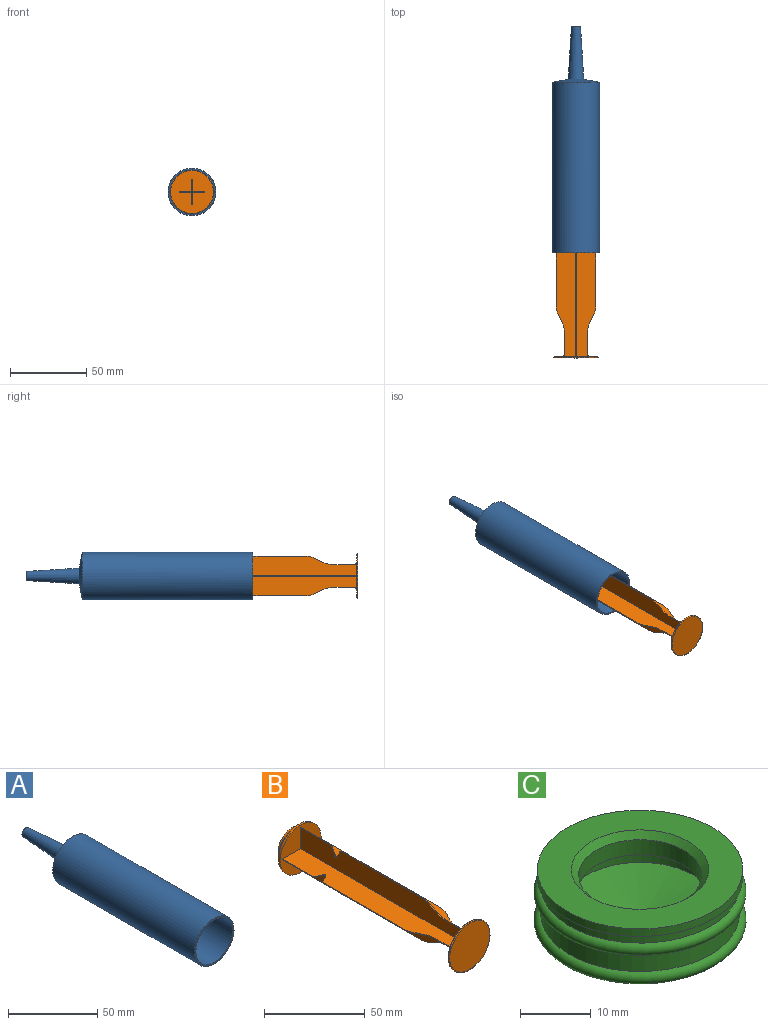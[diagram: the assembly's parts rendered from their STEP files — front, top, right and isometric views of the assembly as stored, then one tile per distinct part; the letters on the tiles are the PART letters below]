
ASSEMBLY  parts=3 mates=2
PART A: 8 faces, bbox 31.2x149x31.2 mm
  f0: cylinder r=14.5mm len=111mm, axis (0,-1,0), area 10112.8mm2, adj f1,f3
  f1: plane 31.2x31.2mm, normal (0,-1,0), area 104mm2, adj f0,f2
  f2: cylinder r=15.6mm len=112.04mm, axis (0,-1,0), area 10981.6mm2, adj f1,f5
  f3: plane 29x29mm, normal (0,-1,0), area 588.1mm2, adj f0,f7
  f4: plane 6x6mm, normal (0,1,0), area 12mm2, adj f6,f7
  f5: cone r=5.5mm half-angle=79deg, axis (0,-1,0), area 694.4mm2, adj f2,f6
  f6: cone r=3mm half-angle=3.5deg, axis (0,-1,0), area 894.5mm2, adj f4,f5
  f7: cone r=4.8mm half-angle=3.8deg, axis (0,-1,0), area 846.6mm2, adj f3,f4
PART B: 103 faces, bbox 31.4x126.4x31.4 mm
  f0: plane 28.8x28.8mm, normal (0,-1,0), area 630.8mm2, adj f4,f5,f17,f23,f61,f62,f63,f64
  f1: plane 20x20mm, normal (0,1,0), area 299.9mm2, adj f2,f3,f28,f30,f35,f36,f37,f38
  f2: plane 8.8x1.47mm, normal (0,0,1), area 6.5mm2, adj f1,f3,f42
  f3: plane 8.8x1.47mm, normal (0.16,0.99,0), area 3.6mm2, adj f1,f2,f30,f48
  f4: plane 118.15x12.8mm, normal (0,0,1), area 1355.9mm2, adj f0,f7,f11,f12,f13,f14,f15,f16
  f5: plane 118.15x12.8mm, normal (0,0,-1), area 1355.9mm2, adj f0,f7,f11,f12,f13,f14,f15,f16
  f6: cylinder r=14.5mm len=29mm, axis (0,-1,0), area 4.6mm2, adj f9,f10
  f7: plane 28.2x28.2mm, normal (0,1,0), area 611.1mm2, adj f4,f5,f10,f11,f61,f62,f63,f64
  f8: plane 28.2x28.2mm, normal (0,-1,0), area 624.6mm2, adj f9
  f9: torus R=14.1mm, axis (0,1,0), area 56.7mm2, adj f6,f8
  f10: torus R=14.1mm, axis (0,1,0), area 56.7mm2, adj f6,f7
  f11: cylinder r=2.28mm len=1.54mm, axis (0,0,-1), area 0.8mm2, adj f4,f5,f7,f12
  f12: plane 14.07x0.4mm, normal (1,0,0), area 5.6mm2, adj f4,f5,f11,f18
  f13: plane 4.67x2.33mm, normal (0.89,-0.45,0), area 2.1mm2, adj f4,f5,f18,f19
  f14: plane 54.93x0.4mm, normal (1,0,0), area 22mm2, adj f4,f5,f19,f22
  f15: plane 4x2.03mm, normal (0.45,0.89,0), area 1.8mm2, adj f4,f5,f20,f22
  f16: plane 4x2.03mm, normal (0.45,-0.89,0), area 1.8mm2, adj f4,f5,f20,f21
  f17: plane 20.47x0.4mm, normal (1,0,0), area 8.2mm2, adj f0,f4,f5,f21
  f18: cylinder r=15mm len=6.71mm, axis (0,0,1), area 2.8mm2, adj f4,f5,f12,f13
  f19: cylinder r=15mm len=6.71mm, axis (0,0,-1), area 2.8mm2, adj f4,f5,f13,f14
  f20: cylinder r=0.8mm len=1.43mm, axis (0,0,-1), area 0.7mm2, adj f4,f5,f15,f16
  f21: cylinder r=2mm len=1.78mm, axis (0,0,-1), area 0.9mm2, adj f4,f5,f16,f17
  f22: cylinder r=2mm len=1.78mm, axis (0,0,1), area 0.9mm2, adj f4,f5,f14,f15
  f23: cylinder r=14.4mm len=28.8mm, axis (0,-1,0), area 108.6mm2, adj f0,f24
  f24: plane 28.8x28.8mm, normal (0,1,0), area 640.1mm2, adj f23,f25,f26,f27,f52,f53,f54,f55
  f25: plane 7x3.7mm, normal (0,0,-1), area 25.9mm2, adj f24,f27,f29,f52
  f26: plane 7x3.7mm, normal (0,0,1), area 25.9mm2, adj f24,f27,f29,f59
  f27: plane 3.7x0.4mm, normal (1,0,0), area 1.5mm2, adj f24,f25,f26,f29
  f28: cylinder r=10mm len=20mm, axis (0,1,0), area 62.8mm2, adj f1,f29
  f29: plane 20x20mm, normal (0,-1,0), area 302.8mm2, adj f25,f26,f27,f28,f52,f53,f54,f55
  f30: plane 8.8x1.47mm, normal (0,0,-1), area 6.5mm2, adj f1,f3,f35
  f31: plane 0.4x0.03mm, normal (-1,0,0), area 0mm2, adj f32,f33,f37
  f32: plane 0.2x0.2mm, normal (0,0.99,0.16), area 0mm2, adj f31,f33,f41
  f33: plane 0.2x0.2mm, normal (0,0.99,-0.16), area 0mm2, adj f31,f32,f34
  f34: plane 0.2x0.2mm, normal (-0.16,0.99,0), area 0mm2, adj f33,f45,f46
  f35: plane 8.8x1.47mm, normal (1,0,0), area 6.5mm2, adj f1,f30,f36
  f36: plane 8.8x1.47mm, normal (0,0.99,-0.16), area 3.6mm2, adj f1,f35,f44,f46
  f37: plane 8.8x1.47mm, normal (-0.16,0.99,0), area 3.6mm2, adj f1,f31,f38,f39
  f38: plane 8.8x1.47mm, normal (0,0,-1), area 6.5mm2, adj f1,f37,f44
  f39: plane 8.8x1.47mm, normal (0,0,1), area 6.5mm2, adj f1,f37,f43
  f40: plane 8.8x1.47mm, normal (0,0.99,0.16), area 3.6mm2, adj f1,f42,f43,f51
  f41: plane 0.2x0.2mm, normal (-0.16,0.99,0), area 0mm2, adj f32,f50,f51
  f42: plane 8.8x1.47mm, normal (1,0,0), area 6.5mm2, adj f1,f2,f40
  f43: plane 8.8x1.47mm, normal (-1,0,0), area 6.5mm2, adj f1,f39,f40
  f44: plane 8.8x1.47mm, normal (-1,0,0), area 6.5mm2, adj f1,f36,f38
  f45: plane 0.2x0.2mm, normal (0.16,0.99,0), area 0mm2, adj f34,f46,f49
  f46: plane 0.4x0.03mm, normal (0,0,-1), area 0mm2, adj f34,f36,f45
  f47: plane 0.2x0.2mm, normal (0,0.99,0.16), area 0mm2, adj f48,f49,f50
  f48: plane 0.4x0.03mm, normal (1,0,0), area 0mm2, adj f3,f47,f49
  f49: plane 0.2x0.2mm, normal (0,0.99,-0.16), area 0mm2, adj f45,f47,f48
  f50: plane 0.2x0.2mm, normal (0.16,0.99,0), area 0mm2, adj f41,f47,f51
  f51: plane 0.4x0.03mm, normal (0,0,1), area 0mm2, adj f40,f41,f50
  f52: plane 7x3.7mm, normal (1,0,0), area 25.9mm2, adj f24,f25,f29,f60
  f53: plane 3.7x0.4mm, normal (0,0,1), area 1.5mm2, adj f24,f29,f57,f59
  f54: plane 7x3.7mm, normal (0,0,-1), area 25.9mm2, adj f24,f29,f55,f58
  f55: plane 3.7x0.4mm, normal (-1,0,0), area 1.5mm2, adj f24,f29,f54,f56
  f56: plane 7x3.7mm, normal (0,0,1), area 25.9mm2, adj f24,f29,f55,f57
  f57: plane 7x3.7mm, normal (-1,0,0), area 25.9mm2, adj f24,f29,f53,f56
  f58: plane 7x3.7mm, normal (-1,0,0), area 25.9mm2, adj f24,f29,f54,f60
  f59: plane 7x3.7mm, normal (1,0,0), area 25.9mm2, adj f24,f26,f29,f53
  f60: plane 3.7x0.4mm, normal (0,0,-1), area 1.5mm2, adj f24,f29,f52,f58
  f61: plane 118.15x12.8mm, normal (-1,0,0), area 1355.9mm2, adj f0,f7,f64,f67,f68,f69,f70,f71
  f62: plane 118.15x12.8mm, normal (-1,0,0), area 1355.9mm2, adj f0,f7,f63,f74,f75,f76,f77,f78
  f63: plane 118.15x12.8mm, normal (0,0,1), area 1355.9mm2, adj f0,f7,f62,f81,f82,f83,f84,f85
  f64: plane 118.15x12.8mm, normal (0,0,-1), area 1355.9mm2, adj f0,f7,f61,f81,f82,f83,f84,f85
  f65: plane 118.15x12.8mm, normal (1,0,0), area 1355.9mm2, adj f0,f5,f7,f67,f68,f69,f70,f71
  f66: plane 118.15x12.8mm, normal (1,0,0), area 1355.9mm2, adj f0,f4,f7,f74,f75,f76,f77,f78
  f67: cylinder r=2.28mm len=1.54mm, axis (-1,0,0), area 0.8mm2, adj f7,f61,f65,f68
  f68: plane 14.07x0.4mm, normal (0,0,-1), area 5.6mm2, adj f61,f65,f67,f88
  f69: plane 4.67x2.33mm, normal (0,-0.45,-0.89), area 2.1mm2, adj f61,f65,f88,f89
  f70: plane 54.93x0.4mm, normal (0,0,-1), area 22mm2, adj f61,f65,f89,f92
  f71: plane 4x2.03mm, normal (0,0.89,-0.45), area 1.8mm2, adj f61,f65,f90,f92
  f72: plane 4x2.03mm, normal (0,-0.89,-0.45), area 1.8mm2, adj f61,f65,f90,f91
  f73: plane 20.47x0.4mm, normal (0,0,-1), area 8.2mm2, adj f0,f61,f65,f91
  f74: cylinder r=2.28mm len=1.54mm, axis (1,0,0), area 0.8mm2, adj f7,f62,f66,f75
  f75: plane 14.07x0.4mm, normal (0,0,1), area 5.6mm2, adj f62,f66,f74,f98
  f76: plane 4.67x2.33mm, normal (0,-0.45,0.89), area 2.1mm2, adj f62,f66,f98,f99
  f77: plane 54.93x0.4mm, normal (0,0,1), area 22mm2, adj f62,f66,f99,f102
  f78: plane 4x2.03mm, normal (0,0.89,0.45), area 1.8mm2, adj f62,f66,f100,f102
  f79: plane 4x2.03mm, normal (0,-0.89,0.45), area 1.8mm2, adj f62,f66,f100,f101
  f80: plane 20.47x0.4mm, normal (0,0,1), area 8.2mm2, adj f0,f62,f66,f101
  f81: plane 20.47x0.4mm, normal (-1,0,0), area 8.2mm2, adj f0,f63,f64,f96
  f82: plane 4x2.03mm, normal (-0.45,-0.89,0), area 1.8mm2, adj f63,f64,f95,f96
  f83: plane 4x2.03mm, normal (-0.45,0.89,0), area 1.8mm2, adj f63,f64,f95,f97
  f84: plane 54.93x0.4mm, normal (-1,0,0), area 22mm2, adj f63,f64,f94,f97
  f85: plane 4.67x2.33mm, normal (-0.89,-0.45,0), area 2.1mm2, adj f63,f64,f93,f94
  f86: plane 14.07x0.4mm, normal (-1,0,0), area 5.6mm2, adj f63,f64,f87,f93
  f87: cylinder r=2.28mm len=1.54mm, axis (0,0,1), area 0.8mm2, adj f7,f63,f64,f86
  f88: cylinder r=15mm len=6.71mm, axis (1,0,0), area 2.8mm2, adj f61,f65,f68,f69
  f89: cylinder r=15mm len=6.71mm, axis (-1,0,0), area 2.8mm2, adj f61,f65,f69,f70
  f90: cylinder r=0.8mm len=1.43mm, axis (-1,0,0), area 0.7mm2, adj f61,f65,f71,f72
  f91: cylinder r=2mm len=1.78mm, axis (-1,0,0), area 0.9mm2, adj f61,f65,f72,f73
  f92: cylinder r=2mm len=1.78mm, axis (1,0,0), area 0.9mm2, adj f61,f65,f70,f71
  f93: cylinder r=15mm len=6.71mm, axis (0,0,-1), area 2.8mm2, adj f63,f64,f85,f86
  f94: cylinder r=15mm len=6.71mm, axis (0,0,1), area 2.8mm2, adj f63,f64,f84,f85
  f95: cylinder r=0.8mm len=1.43mm, axis (0,0,1), area 0.7mm2, adj f63,f64,f82,f83
  f96: cylinder r=2mm len=1.78mm, axis (0,0,1), area 0.9mm2, adj f63,f64,f81,f82
  f97: cylinder r=2mm len=1.78mm, axis (0,0,-1), area 0.9mm2, adj f63,f64,f83,f84
  f98: cylinder r=15mm len=6.71mm, axis (-1,0,0), area 2.8mm2, adj f62,f66,f75,f76
  f99: cylinder r=15mm len=6.71mm, axis (1,0,0), area 2.8mm2, adj f62,f66,f76,f77
  f100: cylinder r=0.8mm len=1.43mm, axis (1,0,0), area 0.7mm2, adj f62,f66,f78,f79
  f101: cylinder r=2mm len=1.78mm, axis (1,0,0), area 0.9mm2, adj f62,f66,f79,f80
  f102: cylinder r=2mm len=1.78mm, axis (-1,0,0), area 0.9mm2, adj f62,f66,f77,f78
PART C: 15 faces, bbox 32.4x32.4x12.8 mm
  f0: cylinder r=10.7mm len=21.4mm, axis (0,0,1), area 183.3mm2, adj f1,f14
  f1: cone r=10.7mm half-angle=76.5deg, axis (0,0,1), area 368.3mm2, adj f0,f2
  f2: sphere r=3mm, area 1.6mm2, adj f1
  f3: sphere r=7mm, area 8.5mm2, adj f4
  f4: cone r=14.23mm half-angle=76.5deg, axis (0,0,1), area 645.1mm2, adj f3,f5
  f5: torus R=14mm, axis (0,0,1), area 255.4mm2, adj f4,f6
  f6: cylinder r=14mm len=28mm, axis (0,0,1), area 263.9mm2, adj f5,f7
  f7: torus R=14mm, axis (0,0,1), area 275.6mm2, adj f6,f8
  f8: cylinder r=14mm len=28mm, axis (0,0,1), area 131.9mm2, adj f7,f9
  f9: plane 29x29mm, normal (0,0,-1), area 44.8mm2, adj f8,f10
  f10: cylinder r=14.5mm len=29mm, axis (0,0,1), area 118.4mm2, adj f9,f11
  f11: plane 29x29mm, normal (0,0,1), area 364.9mm2, adj f10,f12
  f12: cone r=9.7mm half-angle=45deg, axis (0,0,1), area 81.7mm2, adj f11,f13
  f13: cylinder r=8.7mm len=17.4mm, axis (0,0,1), area 142.1mm2, adj f12,f14
  f14: plane 21.4x21.4mm, normal (0,0,-1), area 121.9mm2, adj f0,f13
PLACE A t=(0,-149,0)mm
PLACE B t=(0,-218,0)mm
PLACE C rot(axis=(1,0,0),90deg) t=(0,-97.8,0)mm
MATE fastened C.f12 <-> B.f6  axis (0,-1,0) through (0,-97.8,0)mm
MATE fastened B.f6 <-> A.f0  axis (0,-1,0) through (0,-99,0)mm
